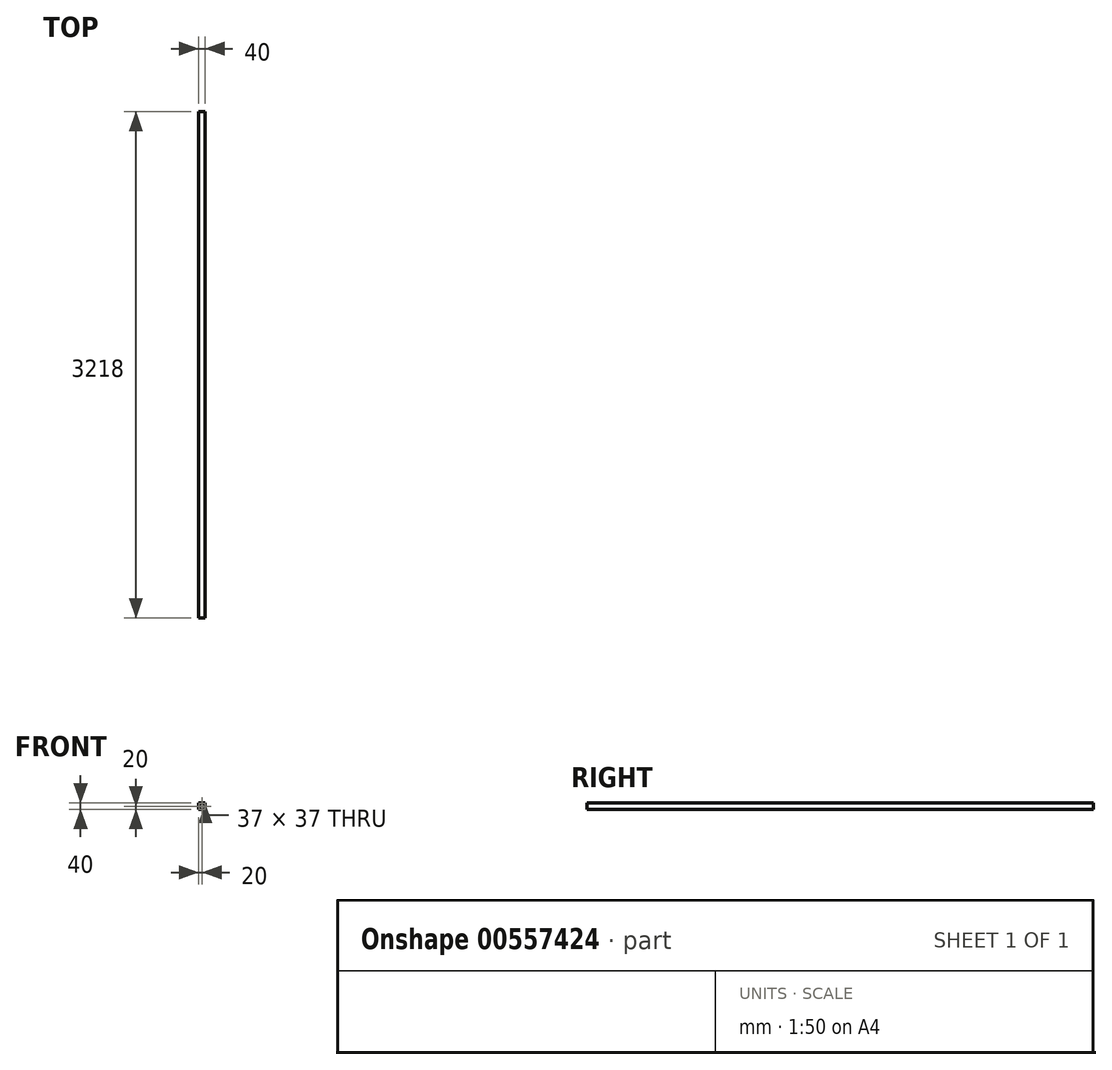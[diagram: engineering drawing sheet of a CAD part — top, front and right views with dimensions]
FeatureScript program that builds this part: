
annotation { "Feature Type Name" : "Feature", "Feature Type Description" : "" }
export const myFeature = defineFeature(function(context is Context, id is Id, definition is map)
    precondition{}
    {
        {
            var Q0;
            Q0=qCreatedBy(makeId("Front.planeOp"),FACE);
            var sketch = newSketch(context, id + "F0", { "sketchPlane" : qUnion([Q0])});
            skLineSegment(sketch, "E0.bottom", {"start": v(20, 20) * mm, "end": v(-20, 20) * mm});
            skLineSegment(sketch, "E0.top", {"start": v(20, -20) * mm, "end": v(-20, -20) * mm});
            skLineSegment(sketch, "E0.left", {"start": v(20, 20) * mm, "end": v(20, -20) * mm});
            skLineSegment(sketch, "E0.right", {"start": v(-20, 20) * mm, "end": v(-20, -20) * mm});
            skPoint(sketch, "E0.middle", {"position": v(0, 0) * mm});
            skLineSegment(sketch, "E1.0", {"start": v(-18.5, 18.5) * mm, "end": v(-18.5, -18.5) * mm});
            skLineSegment(sketch, "E1.1", {"start": v(18.5, 18.5) * mm, "end": v(-18.5, 18.5) * mm});
            skLineSegment(sketch, "E1.2", {"start": v(18.5, 18.5) * mm, "end": v(18.5, -18.5) * mm});
            skLineSegment(sketch, "E1.3", {"start": v(18.5, -18.5) * mm, "end": v(-18.5, -18.5) * mm});
            skSolve(sketch);
        }
        {
            var Q0;
            Q0=makeQuery(id+"F0.imprint","IMPRINT",FACE,{"disambiguationData":[TD([[makeQuery(id+"F0.imprint","IMPRINT",EDGE,{"derivedFrom":sQuery(id+"F0.wireOp",EDGE,"E0.bottom")}),1.0]])]});
            extrude(context, id + "F1", {"entities" : qUnion([Q0]), "endBound" : BoundingType.SYMMETRIC, "depth" : (3220 - 2) * mm, "offsetDistance" : 25 * mm});
        }
    });
